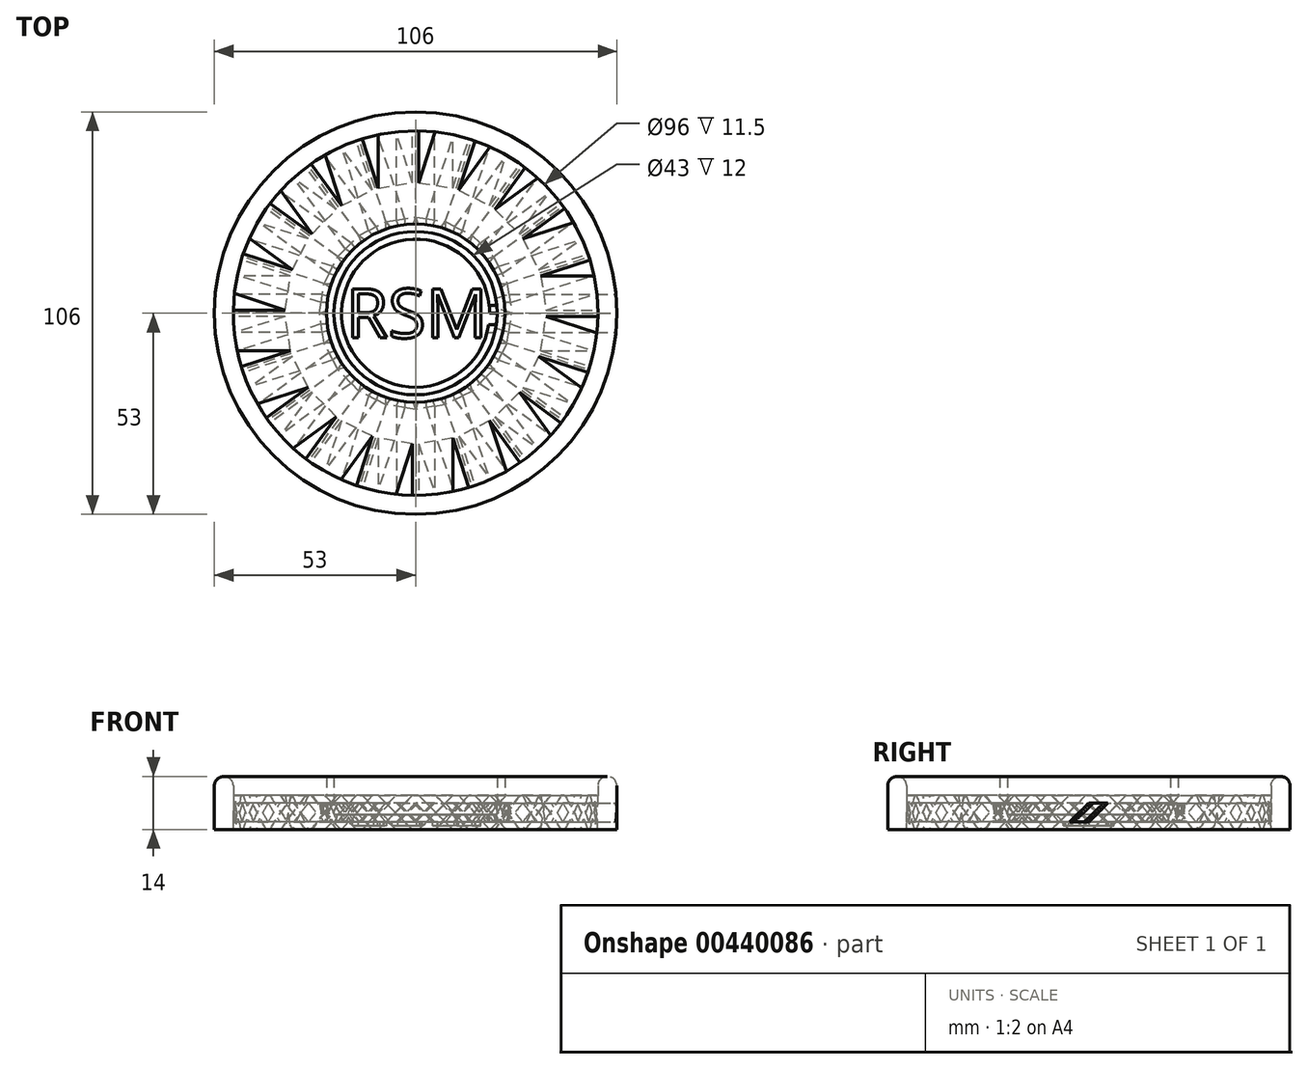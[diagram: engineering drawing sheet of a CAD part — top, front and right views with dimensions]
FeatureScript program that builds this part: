
annotation { "Feature Type Name" : "Feature", "Feature Type Description" : "" }
export const myFeature = defineFeature(function(context is Context, id is Id, definition is map)
    precondition{}
    {
        {
            var Q0;
            Q0=qCreatedBy(makeId("Top.planeOp"),FACE);
            var sketch = newSketch(context, id + "F0", { "sketchPlane" : qUnion([Q0])});
            skCircle(sketch, "E0", {"center": v(0, 0) * mm, "radius": 53 * mm});
            skCircle(sketch, "E1", {"center": v(0, 0) * mm, "radius": 48 * mm});
            skCircle(sketch, "E2", {"center": v(0, 0) * mm, "radius": 19.5 * mm});
            skCircle(sketch, "E3", {"center": v(0, 0) * mm, "radius": 21.5 * mm});
            skCircle(sketch, "E4", {"center": v(0, 0) * mm, "radius": 23.5 * mm});
            skSolve(sketch);
        }
        {
            var Q0;
            Q0=makeQuery(id+"F0.imprint","IMPRINT",FACE,{"disambiguationData":[TD([[makeQuery(id+"F0.imprint","IMPRINT",EDGE,{"derivedFrom":sQuery(id+"F0.wireOp",EDGE,"E0")}),1.0]])]});
            extrude(context, id + "F1", {"entities" : qUnion([Q0]), "depth" : 14 * mm});
        }
        {
            var Q0;
            Q0=makeQuery(id+"F0.imprint","IMPRINT",FACE,{"disambiguationData":[TD([[makeQuery(id+"F0.imprint","IMPRINT",EDGE,{"derivedFrom":sQuery(id+"F0.wireOp",EDGE,"E2")}),-1.0]])]});
            extrude(context, id + "F2", {"entities" : qUnion([Q0]), "depth" : 4 * mm});
        }
        {
            var Q0;
            Q0=makeQuery(id+"F0.imprint","IMPRINT",FACE,{"disambiguationData":[TD([[makeQuery(id+"F0.imprint","IMPRINT",EDGE,{"derivedFrom":sQuery(id+"F0.wireOp",EDGE,"E2")}),1.0]])]});
            extrude(context, id + "F3", {"entities" : qUnion([Q0]), "operationType" : NewBodyOperationType.ADD, "depth" : 2 * mm});
        }
        {
            var Q0;
            Q0=makeQuery(id+"F0.imprint","IMPRINT",FACE,{"disambiguationData":[TD([[makeQuery(id+"F0.imprint","IMPRINT",EDGE,{"derivedFrom":sQuery(id+"F0.wireOp",EDGE,"E3")}),-1.0]])]});
            var Q1;
            Q1=makeQuery(id+"F1.opExtrude","CAP_FACE",FACE,{"disambiguationData":[OSD([sQuery(id+"F0.wireOp",EDGE,"E0"),sQuery(id+"F0.wireOp",EDGE,"E1")])],"isStart":false});
            extrude(context, id + "F4", {"entities" : qUnion([Q0]), "operationType" : NewBodyOperationType.ADD, "endBound" : BoundingType.UP_TO_SURFACE, "endBoundEntityFace" : qUnion([Q1]), "depth" : 25 * mm});
        }
        {
            var Q0;
            Q0=qCreatedBy(makeId("Right.planeOp"),FACE);
            cPlane(context, id + "F5", {"entities" : qUnion([Q0]), "cplaneType" : CPlaneType.OFFSET, "offset" : 53 * mm, "width" : 150 * mm, "height" : 150 * mm});
        }
        {
            var Q0;
            Q0=qCreatedBy(id+"F5.planeOp",FACE);
            var sketch = newSketch(context, id + "F6", { "sketchPlane" : qUnion([Q0])});
            skLineSegment(sketch, "E5.0", {"start": v(-53, 14) * mm, "end": v(53, 14) * mm});
            skLineSegment(sketch, "E6.0", {"start": v(-53, 0) * mm, "end": v(53, 0) * mm});
            skLineSegment(sketch, "E7", {"start": v(-53, 0) * mm, "end": v(-53, 25) * mm});
            skLineSegment(sketch, "E8", {"start": v(53, 25) * mm, "end": v(53, 0) * mm});
            skLineSegment(sketch, "E9", {"start": v(-5, 2) * mm, "end": v(0, 7) * mm});
            skPoint(sketch, "E9.startSnap0", {"position": v(0, 0) * mm});
            skLineSegment(sketch, "E10", {"start": v(0, 7) * mm, "end": v(5, 7) * mm});
            skLineSegment(sketch, "E11", {"start": v(5, 7) * mm, "end": v(0, 2) * mm});
            skLineSegment(sketch, "E12", {"start": v(0, 2) * mm, "end": v(-5, 2) * mm});
            skLineSegment(sketch, "E13.0", {"start": v(-9.83, 0) * mm, "end": v(-0.83, 9) * mm});
            skLineSegment(sketch, "E13.1", {"start": v(0.83, 0) * mm, "end": v(-9.83, 0) * mm});
            skLineSegment(sketch, "E13.2", {"start": v(9.83, 9) * mm, "end": v(0.83, 0) * mm});
            skLineSegment(sketch, "E13.3", {"start": v(-0.83, 9) * mm, "end": v(9.83, 9) * mm});
            skLineSegment(sketch, "E14", {"start": v(0, 7) * mm, "end": v(0, -17.8) * mm, "construction": true});
            skSolve(sketch);
        }
        {
            var Q0;
            Q0=makeQuery(id+"F6.imprint","IMPRINT",FACE,{"disambiguationData":[TD([[makeQuery(id+"F6.imprint","IMPRINT",EDGE,{"derivedFrom":sQuery(id+"F6.wireOp",EDGE,"E9")}),1.0]])]});
            var Q1;
            Q1=makeQuery(id+"F4.opExtrude","SWEPT_FACE",FACE,{"disambiguationData":[OSD([sQuery(id+"F0.wireOp",EDGE,"E3")])]});
            var Q2;
            Q2=makeQuery(id+"F1.opExtrude","SWEPT_FACE",FACE,{"disambiguationData":[OSD([sQuery(id+"F0.wireOp",EDGE,"E0")])]});
            extrude(context, id + "F7", {"entities" : qUnion([Q0]), "endBound" : BoundingType.UP_TO_SURFACE, "oppositeDirection" : true, "endBoundEntityFace" : qUnion([Q1]), "depth" : 25 * mm, "hasSecondDirection" : true, "secondDirectionBound" : SecondDirectionBoundingType.UP_TO_SURFACE, "secondDirectionOppositeDirection" : true, "secondDirectionBoundEntityFace" : qUnion([Q2]), "secondDirectionDepth" : 25 * mm});
        }
        {
            var Q0;
            Q0=makeQuery(id+"F6.imprint","IMPRINT",FACE,{"disambiguationData":[TD([[makeQuery(id+"F6.imprint","IMPRINT",EDGE,{"derivedFrom":sQuery(id+"F6.wireOp",EDGE,"E9")}),-1.0]])]});
            var Q1;
            Q1=makeQuery(id+"F4.opExtrude","SWEPT_FACE",FACE,{"disambiguationData":[OSD([sQuery(id+"F0.wireOp",EDGE,"E3")])]});
            extrude(context, id + "F8", {"entities" : qUnion([Q0]), "operationType" : NewBodyOperationType.REMOVE, "oppositeDirection" : true, "endBoundEntityFace" : qUnion([Q1]), "depth" : 42.9 * mm});
        }
        {
            assignVariable(context, id + "F9", {"name" : "Repeats", "anyValue" : 20});
        }
        {
            var Q0;
            Q0=makeQuery(id+"F7.opExtrude","SWEPT_BODY",BODY,{"disambiguationData":[OSD([sQuery(id+"F6.wireOp",EDGE,"E9"),sQuery(id+"F6.wireOp",EDGE,"E10"),sQuery(id+"F6.wireOp",EDGE,"E11"),sQuery(id+"F6.wireOp",EDGE,"E12"),sQuery(id+"F6.wireOp",EDGE,"E13.0"),sQuery(id+"F6.wireOp",EDGE,"E13.1"),sQuery(id+"F6.wireOp",EDGE,"E13.2"),sQuery(id+"F6.wireOp",EDGE,"E13.3")])]});
            var Q1;
            Q1=sQuery(id+"F0.wireOp",EDGE,"E1");
            circularPattern(context, id + "F10", {"operationType" : NewBodyOperationType.ADD, "entities" : qUnion([Q0]), "axis" : qUnion([Q1]), "angle" : 360 * degree, "instanceCount" : getVariable(context, 'Repeats'), "equalSpace" : true});
        }
        {
            var Q0;
            Q0=makeQuery(id+"F1.opExtrude","CAP_EDGE",EDGE,{"disambiguationData":[OSD([sQuery(id+"F0.wireOp",EDGE,"E0")])],"isStart":false});
            var Q1;
            Q1=makeQuery(id+"F1.opExtrude","CAP_EDGE",EDGE,{"disambiguationData":[OSD([sQuery(id+"F0.wireOp",EDGE,"E1")])],"isStart":false});
            fillet(context, id + "F11", {"entities" : qUnion([Q0, Q1]), "radius" : 2.5 * mm, "tangentPropagation" : true, "allowEdgeOverflow" : false});
        }
        {
            var Q0;
            {var subQ0=sQuery(id+"F6.wireOp",EDGE,"E12");var subQ1=makeQuery(id+"F7.opExtrude","SWEPT_FACE",FACE,{"disambiguationData":[OSD([subQ0])]});var subQ2=makeQuery(id+"F8.opExtrude","SWEPT_FACE",FACE,{"disambiguationData":[OSD([subQ0])]});Q0=makeQuery(id+"FizsFxfSYBGIyEo_1.19.F8.boolean.opBoolean","MERGE",FACE,{"derivedFrom":[makeQuery(id+"F10.opPattern","COPY",FACE,{"derivedFrom":subQ1,"instanceName":"1"}),makeQuery(id+"FizsFxfSYBGIyEo_1.18.F8.boolean.opBoolean","MERGE",FACE,{"derivedFrom":[makeQuery(id+"F10.opPattern","COPY",FACE,{"derivedFrom":subQ1,"instanceName":"2"}),makeQuery(id+"FizsFxfSYBGIyEo_1.17.F8.boolean.opBoolean","MERGE",FACE,{"derivedFrom":[makeQuery(id+"F10.opPattern","COPY",FACE,{"derivedFrom":subQ1,"instanceName":"3"}),makeQuery(id+"FizsFxfSYBGIyEo_1.16.F8.boolean.opBoolean","MERGE",FACE,{"derivedFrom":[makeQuery(id+"F10.opPattern","COPY",FACE,{"derivedFrom":subQ1,"instanceName":"4"}),makeQuery(id+"FizsFxfSYBGIyEo_1.15.F8.boolean.opBoolean","MERGE",FACE,{"derivedFrom":[makeQuery(id+"F10.opPattern","COPY",FACE,{"derivedFrom":subQ1,"instanceName":"5"}),makeQuery(id+"FizsFxfSYBGIyEo_1.14.F8.boolean.opBoolean","MERGE",FACE,{"derivedFrom":[makeQuery(id+"F10.opPattern","COPY",FACE,{"derivedFrom":subQ1,"instanceName":"6"}),makeQuery(id+"FizsFxfSYBGIyEo_1.13.F8.boolean.opBoolean","MERGE",FACE,{"derivedFrom":[makeQuery(id+"F10.opPattern","COPY",FACE,{"derivedFrom":subQ1,"instanceName":"7"}),makeQuery(id+"FizsFxfSYBGIyEo_1.12.F8.boolean.opBoolean","MERGE",FACE,{"derivedFrom":[makeQuery(id+"F10.opPattern","COPY",FACE,{"derivedFrom":subQ1,"instanceName":"8"}),makeQuery(id+"FizsFxfSYBGIyEo_1.11.F8.boolean.opBoolean","MERGE",FACE,{"derivedFrom":[makeQuery(id+"F10.opPattern","COPY",FACE,{"derivedFrom":subQ1,"instanceName":"9"}),makeQuery(id+"FizsFxfSYBGIyEo_1.10.F8.boolean.opBoolean","MERGE",FACE,{"derivedFrom":[makeQuery(id+"F10.opPattern","COPY",FACE,{"derivedFrom":subQ1,"instanceName":"10"}),makeQuery(id+"FizsFxfSYBGIyEo_1.9.F8.boolean.opBoolean","MERGE",FACE,{"derivedFrom":[makeQuery(id+"F10.opPattern","COPY",FACE,{"derivedFrom":subQ1,"instanceName":"11"}),makeQuery(id+"FizsFxfSYBGIyEo_1.8.F8.boolean.opBoolean","MERGE",FACE,{"derivedFrom":[makeQuery(id+"F10.opPattern","COPY",FACE,{"derivedFrom":subQ1,"instanceName":"12"}),makeQuery(id+"FizsFxfSYBGIyEo_1.7.F8.boolean.opBoolean","MERGE",FACE,{"derivedFrom":[makeQuery(id+"F10.opPattern","COPY",FACE,{"derivedFrom":subQ1,"instanceName":"13"}),makeQuery(id+"FizsFxfSYBGIyEo_1.6.F8.boolean.opBoolean","MERGE",FACE,{"derivedFrom":[makeQuery(id+"F10.opPattern","COPY",FACE,{"derivedFrom":subQ1,"instanceName":"14"}),makeQuery(id+"FizsFxfSYBGIyEo_1.5.F8.boolean.opBoolean","MERGE",FACE,{"derivedFrom":[makeQuery(id+"F10.opPattern","COPY",FACE,{"derivedFrom":subQ1,"instanceName":"15"}),makeQuery(id+"FizsFxfSYBGIyEo_1.4.F8.boolean.opBoolean","MERGE",FACE,{"derivedFrom":[makeQuery(id+"F10.opPattern","COPY",FACE,{"derivedFrom":subQ1,"instanceName":"16"}),makeQuery(id+"FizsFxfSYBGIyEo_1.3.F8.boolean.opBoolean","MERGE",FACE,{"derivedFrom":[makeQuery(id+"F10.opPattern","COPY",FACE,{"derivedFrom":subQ1,"instanceName":"17"}),makeQuery(id+"FizsFxfSYBGIyEo_1.2.F8.boolean.opBoolean","MERGE",FACE,{"derivedFrom":[makeQuery(id+"F10.opPattern","COPY",FACE,{"derivedFrom":subQ1,"instanceName":"18"}),makeQuery(id+"FizsFxfSYBGIyEo_1.1.F8.boolean.opBoolean","MERGE",FACE,{"derivedFrom":[makeQuery(id+"F10.boolean.opBoolean","MERGE",FACE,{"derivedFrom":[subQ1,makeQuery(id+"F8.boolean.opBoolean","MERGE",FACE,{"derivedFrom":[makeQuery(id+"F3.opExtrude","CAP_FACE",FACE,{"disambiguationData":[OSD([sQuery(id+"F0.wireOp",EDGE,"E2")])],"isStart":false}),subQ2]}),makeQuery(id+"F8.boolean.opBoolean","COPY",FACE,{"derivedFrom":subQ2})]}),makeQuery(id+"F10.opPattern","COPY",FACE,{"derivedFrom":subQ1,"instanceName":"19"}),makeQuery(id+"FizsFxfSYBGIyEo_1.1.F8.opExtrude","SWEPT_FACE",FACE,{"disambiguationData":[OSD([subQ0])]})]}),makeQuery(id+"FizsFxfSYBGIyEo_1.2.F8.opExtrude","SWEPT_FACE",FACE,{"disambiguationData":[OSD([subQ0])]})]}),makeQuery(id+"FizsFxfSYBGIyEo_1.3.F8.opExtrude","SWEPT_FACE",FACE,{"disambiguationData":[OSD([subQ0])]})]}),makeQuery(id+"FizsFxfSYBGIyEo_1.4.F8.opExtrude","SWEPT_FACE",FACE,{"disambiguationData":[OSD([subQ0])]})]}),makeQuery(id+"FizsFxfSYBGIyEo_1.5.F8.opExtrude","SWEPT_FACE",FACE,{"disambiguationData":[OSD([subQ0])]})]}),makeQuery(id+"FizsFxfSYBGIyEo_1.6.F8.opExtrude","SWEPT_FACE",FACE,{"disambiguationData":[OSD([subQ0])]})]}),makeQuery(id+"FizsFxfSYBGIyEo_1.7.F8.opExtrude","SWEPT_FACE",FACE,{"disambiguationData":[OSD([subQ0])]})]}),makeQuery(id+"FizsFxfSYBGIyEo_1.8.F8.opExtrude","SWEPT_FACE",FACE,{"disambiguationData":[OSD([subQ0])]})]}),makeQuery(id+"FizsFxfSYBGIyEo_1.9.F8.opExtrude","SWEPT_FACE",FACE,{"disambiguationData":[OSD([subQ0])]})]}),makeQuery(id+"FizsFxfSYBGIyEo_1.10.F8.opExtrude","SWEPT_FACE",FACE,{"disambiguationData":[OSD([subQ0])]})]}),makeQuery(id+"FizsFxfSYBGIyEo_1.11.F8.opExtrude","SWEPT_FACE",FACE,{"disambiguationData":[OSD([subQ0])]})]}),makeQuery(id+"FizsFxfSYBGIyEo_1.12.F8.opExtrude","SWEPT_FACE",FACE,{"disambiguationData":[OSD([subQ0])]})]}),makeQuery(id+"FizsFxfSYBGIyEo_1.13.F8.opExtrude","SWEPT_FACE",FACE,{"disambiguationData":[OSD([subQ0])]})]}),makeQuery(id+"FizsFxfSYBGIyEo_1.14.F8.opExtrude","SWEPT_FACE",FACE,{"disambiguationData":[OSD([subQ0])]})]}),makeQuery(id+"FizsFxfSYBGIyEo_1.15.F8.opExtrude","SWEPT_FACE",FACE,{"disambiguationData":[OSD([subQ0])]})]}),makeQuery(id+"FizsFxfSYBGIyEo_1.16.F8.opExtrude","SWEPT_FACE",FACE,{"disambiguationData":[OSD([subQ0])]})]}),makeQuery(id+"FizsFxfSYBGIyEo_1.17.F8.opExtrude","SWEPT_FACE",FACE,{"disambiguationData":[OSD([subQ0])]})]}),makeQuery(id+"FizsFxfSYBGIyEo_1.18.F8.opExtrude","SWEPT_FACE",FACE,{"disambiguationData":[OSD([subQ0])]})]}),makeQuery(id+"FizsFxfSYBGIyEo_1.19.F8.opExtrude","SWEPT_FACE",FACE,{"disambiguationData":[OSD([subQ0])]})]});}
            var sketch = newSketch(context, id + "F12", { "sketchPlane" : qUnion([Q0])});
            skCircle(sketch, "E15.0", {"center": v(0, 0) * mm, "radius": 19.5 * mm, "construction": true});
            skText(sketch, "E16", { "text": "RSM", "fontName": "OpenSans-Regular.ttf"});
            const initialGuessF12  = {"E16": [-0.01839, -0.0065, 1, 0, 0.013]};
            skSetInitialGuess(sketch, initialGuessF12);
            skSolve(sketch);
        }
        {
            var Q0;
            Q0 = qSketchRegion(id + "F12", true);
            extrude(context, id + "F13", {"entities" : qUnion([Q0]), "operationType" : NewBodyOperationType.REMOVE, "oppositeDirection" : true, "depth" : 1 * mm});
        }
    });
